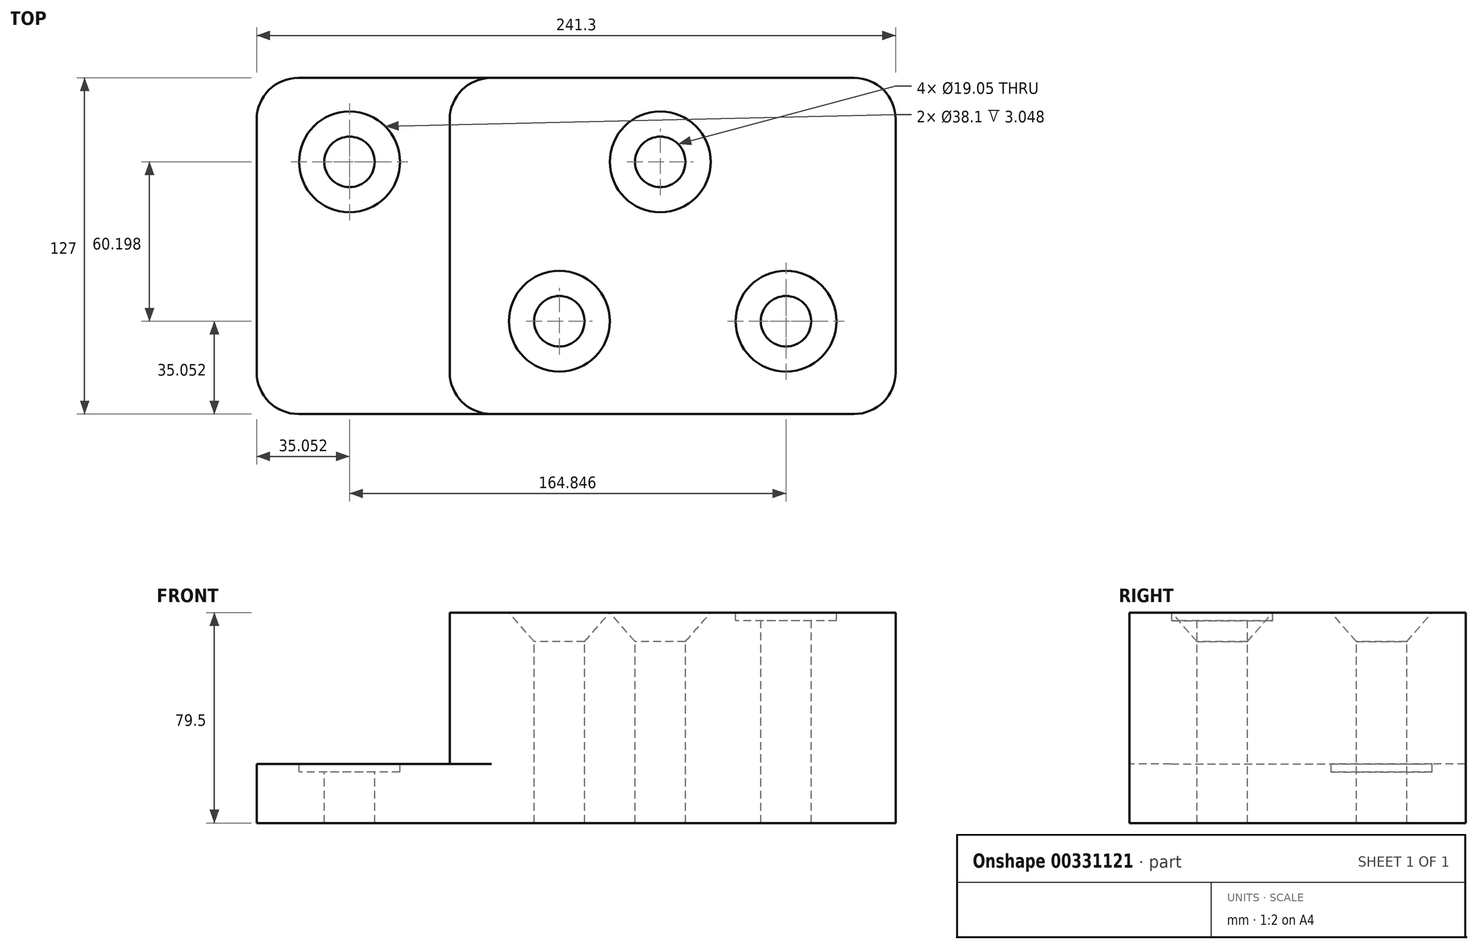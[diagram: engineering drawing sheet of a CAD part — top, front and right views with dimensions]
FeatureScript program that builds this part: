
annotation { "Feature Type Name" : "Feature", "Feature Type Description" : "" }
export const myFeature = defineFeature(function(context is Context, id is Id, definition is map)
    precondition{}
    {
        {
            var Q0;
            Q0=qCreatedBy(makeId("Top.planeOp"),FACE);
            var sketch = newSketch(context, id + "F0", { "sketchPlane" : qUnion([Q0])});
            skLineSegment(sketch, "E0", {"start": v(0, 0) * mm, "end": v(0, 127) * mm});
            skLineSegment(sketch, "E1", {"start": v(0, 127) * mm, "end": v(241.3, 127) * mm});
            skLineSegment(sketch, "E2", {"start": v(241.3, 127) * mm, "end": v(241.3, 0) * mm});
            skLineSegment(sketch, "E3", {"start": v(241.3, 0) * mm, "end": v(0, 0) * mm});
            skPoint(sketch, "E4", {"position": v(35.05, 95.25) * mm});
            skSolve(sketch);
        }
        {
            var Q0;
            Q0=makeQuery(id+"F0.imprint","IMPRINT",FACE,{"disambiguationData":[TD([[makeQuery(id+"F0.imprint","IMPRINT",EDGE,{"derivedFrom":sQuery(id+"F0.wireOp",EDGE,"E0")}),-1.0]])]});
            extrude(context, id + "F1", {"entities" : qUnion([Q0]), "oppositeDirection" : true, "depth" : 22.35 * mm});
        }
        {
            var Q0;
            Q0=sQuery(id+"F0.wireOp",VERTEX,"E4");
            var Q1;
            Q1=makeQuery(id+"F1.opExtrude","SWEPT_BODY",BODY,{"disambiguationData":[OSD([sQuery(id+"F0.wireOp",EDGE,"E0"),sQuery(id+"F0.wireOp",EDGE,"E1"),sQuery(id+"F0.wireOp",EDGE,"E2"),sQuery(id+"F0.wireOp",EDGE,"E3")])]});
            hole(context, id + "F2", {"style" : HoleStyle.C_BORE, "endStyle" : HoleEndStyle.THROUGH, "holeDiameter" : 19.05 * mm, "cBoreDiameter" : 38.1 * mm, "cBoreDepth" : 3.05 * mm, "tappedDepth" : 12.7 * mm, "tapClearance" : 3, "locations" : qUnion([Q0]), "scope" : qUnion([Q1])});
        }
        {
            var Q0;
            Q0=makeQuery(id+"F1.opExtrude","CAP_FACE",FACE,{"disambiguationData":[OSD([sQuery(id+"F0.wireOp",EDGE,"E0"),sQuery(id+"F0.wireOp",EDGE,"E1"),sQuery(id+"F0.wireOp",EDGE,"E2"),sQuery(id+"F0.wireOp",EDGE,"E3")])],"isStart":true});
            var sketch = newSketch(context, id + "F3", { "sketchPlane" : qUnion([Q0])});
            skLineSegment(sketch, "E5", {"start": v(241.3, 127) * mm, "end": v(72.9, 127) * mm});
            skLineSegment(sketch, "E6", {"start": v(72.9, 127) * mm, "end": v(72.9, 0) * mm});
            skLineSegment(sketch, "E7", {"start": v(72.9, 0) * mm, "end": v(241.3, 0) * mm});
            skLineSegment(sketch, "E8", {"start": v(241.3, 0) * mm, "end": v(241.3, 127) * mm});
            skSolve(sketch);
        }
        {
            var Q0;
            Q0 = qSketchRegion(id + "F3", true);
            extrude(context, id + "F4", {"entities" : qUnion([Q0]), "operationType" : NewBodyOperationType.ADD, "depth" : 57.15 * mm});
        }
        {
            var Q0;
            Q0=makeQuery(id+"F4.opExtrude","CAP_FACE",FACE,{"disambiguationData":[OSD([sQuery(id+"F3.wireOp",EDGE,"E5"),sQuery(id+"F3.wireOp",EDGE,"E6"),sQuery(id+"F3.wireOp",EDGE,"E7"),sQuery(id+"F3.wireOp",EDGE,"E8")])],"isStart":false});
            var sketch = newSketch(context, id + "F5", { "sketchPlane" : qUnion([Q0])});
            skPoint(sketch, "E9", {"position": v(152.4, 95.25) * mm});
            skPoint(sketch, "E10", {"position": v(114.3, 35.05) * mm});
            skPoint(sketch, "E11", {"position": v(199.9, 35.05) * mm});
            skSolve(sketch);
        }
        {
            var Q0;
            Q0=sQuery(id+"F5.wireOp",VERTEX,"E11");
            var Q1;
            Q1=makeQuery(id+"F1.opExtrude","SWEPT_BODY",BODY,{"disambiguationData":[OSD([sQuery(id+"F0.wireOp",EDGE,"E0"),sQuery(id+"F0.wireOp",EDGE,"E1"),sQuery(id+"F0.wireOp",EDGE,"E2"),sQuery(id+"F0.wireOp",EDGE,"E3")])]});
            hole(context, id + "F6", {"style" : HoleStyle.C_BORE, "endStyle" : HoleEndStyle.THROUGH, "holeDiameter" : 19.05 * mm, "cBoreDiameter" : 38.1 * mm, "cBoreDepth" : 3.05 * mm, "tappedDepth" : 12.7 * mm, "tapClearance" : 3, "locations" : qUnion([Q0]), "scope" : qUnion([Q1])});
        }
        {
            var Q0;
            Q0=sQuery(id+"F5.wireOp",VERTEX,"E9");
            var Q1;
            Q1=makeQuery(id+"F1.opExtrude","SWEPT_BODY",BODY,{"disambiguationData":[OSD([sQuery(id+"F0.wireOp",EDGE,"E0"),sQuery(id+"F0.wireOp",EDGE,"E1"),sQuery(id+"F0.wireOp",EDGE,"E2"),sQuery(id+"F0.wireOp",EDGE,"E3")])]});
            hole(context, id + "F7", {"style" : HoleStyle.C_SINK, "endStyle" : HoleEndStyle.THROUGH, "holeDiameter" : 19.05 * mm, "cSinkDiameter" : 38.1 * mm, "cSinkAngle" : 82 * degree, "tappedDepth" : 12.7 * mm, "tapClearance" : 3, "locations" : qUnion([Q0]), "scope" : qUnion([Q1])});
        }
        {
            var Q0;
            Q0=sQuery(id+"F5.wireOp",VERTEX,"E10");
            var Q1;
            Q1=makeQuery(id+"F1.opExtrude","SWEPT_BODY",BODY,{"disambiguationData":[OSD([sQuery(id+"F0.wireOp",EDGE,"E0"),sQuery(id+"F0.wireOp",EDGE,"E1"),sQuery(id+"F0.wireOp",EDGE,"E2"),sQuery(id+"F0.wireOp",EDGE,"E3")])]});
            hole(context, id + "F8", {"style" : HoleStyle.C_SINK, "endStyle" : HoleEndStyle.THROUGH, "holeDiameter" : 19.05 * mm, "cSinkDiameter" : 38.1 * mm, "cSinkAngle" : 82 * degree, "tappedDepth" : 12.7 * mm, "tapClearance" : 3, "locations" : qUnion([Q0]), "scope" : qUnion([Q1])});
        }
        {
            var Q0;
            Q0=makeQuery(id+"F1.opExtrude","SWEPT_EDGE",EDGE,{"disambiguationData":[OSD([sQuery(id+"F0.wireOp",EDGE,"E0"),sQuery(id+"F0.wireOp",EDGE,"E1")])]});
            var Q1;
            Q1=makeQuery(id+"F1.opExtrude","SWEPT_EDGE",EDGE,{"disambiguationData":[OSD([sQuery(id+"F0.wireOp",EDGE,"E0"),sQuery(id+"F0.wireOp",EDGE,"E3")])]});
            var Q2;
            Q2=makeQuery(id+"F4.opExtrude","SWEPT_EDGE",EDGE,{"disambiguationData":[OSD([sQuery(id+"F0.wireOp",EDGE,"E1"),sQuery(id+"F3.wireOp",EDGE,"E5"),sQuery(id+"F3.wireOp",EDGE,"E6")])]});
            var Q3;
            Q3=makeQuery(id+"F4.opExtrude","SWEPT_EDGE",EDGE,{"disambiguationData":[OSD([sQuery(id+"F0.wireOp",EDGE,"E3"),sQuery(id+"F3.wireOp",EDGE,"E6"),sQuery(id+"F3.wireOp",EDGE,"E7")])]});
            var Q4;
            Q4=makeQuery(id+"F4.boolean.opBoolean","MERGE",EDGE,{"derivedFrom":[makeQuery(id+"F1.opExtrude","SWEPT_EDGE",EDGE,{"disambiguationData":[OSD([sQuery(id+"F0.wireOp",EDGE,"E1"),sQuery(id+"F0.wireOp",EDGE,"E2")])]}),makeQuery(id+"F4.opExtrude","SWEPT_EDGE",EDGE,{"disambiguationData":[OSD([sQuery(id+"F3.wireOp",EDGE,"E5"),sQuery(id+"F3.wireOp",EDGE,"E8")])]})]});
            var Q5;
            Q5=makeQuery(id+"F4.boolean.opBoolean","MERGE",EDGE,{"derivedFrom":[makeQuery(id+"F1.opExtrude","SWEPT_EDGE",EDGE,{"disambiguationData":[OSD([sQuery(id+"F0.wireOp",EDGE,"E2"),sQuery(id+"F0.wireOp",EDGE,"E3")])]}),makeQuery(id+"F4.opExtrude","SWEPT_EDGE",EDGE,{"disambiguationData":[OSD([sQuery(id+"F3.wireOp",EDGE,"E7"),sQuery(id+"F3.wireOp",EDGE,"E8")])]})]});
            fillet(context, id + "F9", {"entities" : qUnion([Q0, Q1, Q2, Q3, Q4, Q5]), "radius" : 15.75 * mm, "tangentPropagation" : true, "allowEdgeOverflow" : false});
        }
    });
